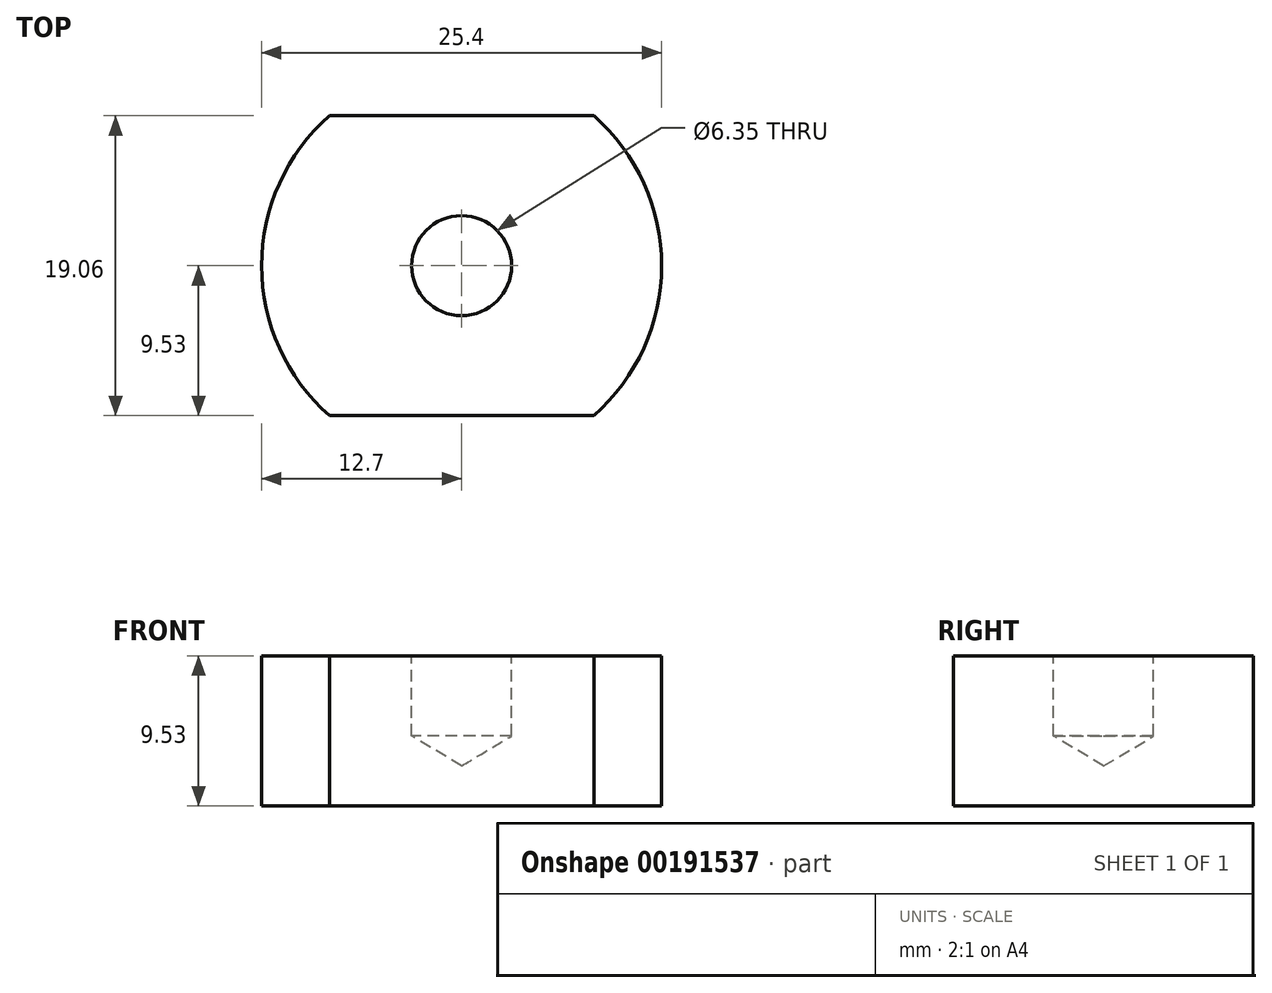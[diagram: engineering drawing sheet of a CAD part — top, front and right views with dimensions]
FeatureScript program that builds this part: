
annotation { "Feature Type Name" : "Feature", "Feature Type Description" : "" }
export const myFeature = defineFeature(function(context is Context, id is Id, definition is map)
    precondition{}
    {
        {
            var Q0;
            Q0=qCreatedBy(makeId("Top.planeOp"),FACE);
            var sketch = newSketch(context, id + "F0", { "sketchPlane" : qUnion([Q0])});
            skCircle(sketch, "E0", {"center": v(0, 0) * mm, "radius": 12.7 * mm});
            skSolve(sketch);
        }
        {
            var Q0;
            {var subQ5=sQuery(id+"F0.wireOp",EDGE,"z13BtfAA-yw19-YVnG-XlrF-XeZV8wihE7Pf.bottom");Q0=makeQuery(id+"F0.imprint","IMPRINT",FACE,{"disambiguationData":[TD([[makeQuery(id+"F0.imprint","IMPRINT",EDGE,{"derivedFrom":subQ5}),1.0]])]});}
            var Q1;
            Q1=makeQuery(id+"F0.imprint","IMPRINT",FACE,{"disambiguationData":[TD([[makeQuery(id+"F0.imprint","IMPRINT",EDGE,{"derivedFrom":sQuery(id+"F0.wireOp",EDGE,"E0")}),1.0]])]});
            extrude(context, id + "F1", {"entities" : qUnion([Q0, Q1]), "depth" : 9.52 * mm});
        }
        {
            var Q0;
            Q0=makeQuery(id+"F1.opExtrude","CAP_FACE",FACE,{"disambiguationData":[OSD([sQuery(id+"F0.wireOp",EDGE,"E0")])],"isStart":false});
            var sketch = newSketch(context, id + "F2", { "sketchPlane" : qUnion([Q0])});
            skPoint(sketch, "E1", {"position": v(0, 0) * mm});
            skSolve(sketch);
        }
        {
            var Q0;
            Q0=sQuery(id+"F2.wireOp",VERTEX,"E1");
            var Q1;
            Q1=makeQuery(id+"F1.opExtrude","SWEPT_BODY",BODY,{"disambiguationData":[OSD([sQuery(id+"F0.wireOp",EDGE,"E0")])]});
            hole(context, id + "F3", {"style" : HoleStyle.SIMPLE, "endStyle" : HoleEndStyle.BLIND, "holeDiameter" : 6.35 * mm, "holeDepth" : 5.08 * mm, "startFromSketch" : true, "locations" : qUnion([Q0]), "scope" : qUnion([Q1])});
        }
        {
            var Q0;
            Q0=makeQuery(id+"F1.opExtrude","CAP_FACE",FACE,{"disambiguationData":[OSD([sQuery(id+"F0.wireOp",EDGE,"E0")])],"isStart":false});
            var sketch = newSketch(context, id + "F4", { "sketchPlane" : qUnion([Q0])});
            skLineSegment(sketch, "E2.bottom", {"start": v(19.05, 9.53) * mm, "end": v(-19.05, 9.53) * mm});
            skLineSegment(sketch, "E2.top", {"start": v(19.05, -9.53) * mm, "end": v(-19.05, -9.53) * mm});
            skLineSegment(sketch, "E2.left", {"start": v(19.05, 9.53) * mm, "end": v(19.05, -9.53) * mm});
            skLineSegment(sketch, "E2.right", {"start": v(-19.05, 9.53) * mm, "end": v(-19.05, -9.53) * mm});
            skPoint(sketch, "E2.middle", {"position": v(0, 0) * mm});
            skSolve(sketch);
        }
        {
            var Q0;
            {var subQ0=sQuery(id+"F4.wireOp",EDGE,"E2.left");Q0=makeQuery(id+"F4.imprint","IMPRINT",FACE,{"disambiguationData":[TD([[makeQuery(id+"F4.imprint","IMPRINT",EDGE,{"derivedFrom":subQ0}),-1.0]])]});}
            var Q1;
            {var subQ0=sQuery(id+"F4.wireOp",EDGE,"E2.right");Q1=makeQuery(id+"F4.imprint","IMPRINT",FACE,{"disambiguationData":[TD([[makeQuery(id+"F4.imprint","IMPRINT",EDGE,{"derivedFrom":subQ0}),1.0]])]});}
            var Q2;
            {var subQ0=sQuery(id+"F4.wireOp",EDGE,"E2.top");var subQ1=makeQuery(id+"F1.opExtrude","CAP_EDGE",EDGE,{"disambiguationData":[OSD([sQuery(id+"F0.wireOp",EDGE,"E0")])],"isStart":false});var subQ2=makeQuery(id+"F4.imprint","INTERSECT",VERTEX,{"disambiguationData":[OD(0.0)],"derivedFrom":[subQ1,subQ0]});Q2=makeQuery(id+"F4.imprint","IMPRINT",FACE,{"disambiguationData":[TD([[makeQuery(id+"F4.imprint","IMPRINT",EDGE,{"disambiguationData":[TD([[subQ2,-1.0]])],"derivedFrom":subQ0}),1.0]])]});}
            var Q3;
            {var subQ0=sQuery(id+"F4.wireOp",EDGE,"E2.bottom");var subQ1=makeQuery(id+"F1.opExtrude","CAP_EDGE",EDGE,{"disambiguationData":[OSD([sQuery(id+"F0.wireOp",EDGE,"E0")])],"isStart":false});var subQ2=makeQuery(id+"F4.imprint","INTERSECT",VERTEX,{"disambiguationData":[OD(0.0)],"derivedFrom":[subQ1,subQ0]});Q3=makeQuery(id+"F4.imprint","IMPRINT",FACE,{"disambiguationData":[TD([[makeQuery(id+"F4.imprint","IMPRINT",EDGE,{"disambiguationData":[TD([[subQ2,-1.0]])],"derivedFrom":subQ0}),-1.0]])]});}
            extrude(context, id + "F5", {"entities" : qUnion([Q0, Q1, Q2, Q3]), "operationType" : NewBodyOperationType.REMOVE, "oppositeDirection" : true, "depth" : 25.4 * mm});
        }
    });
